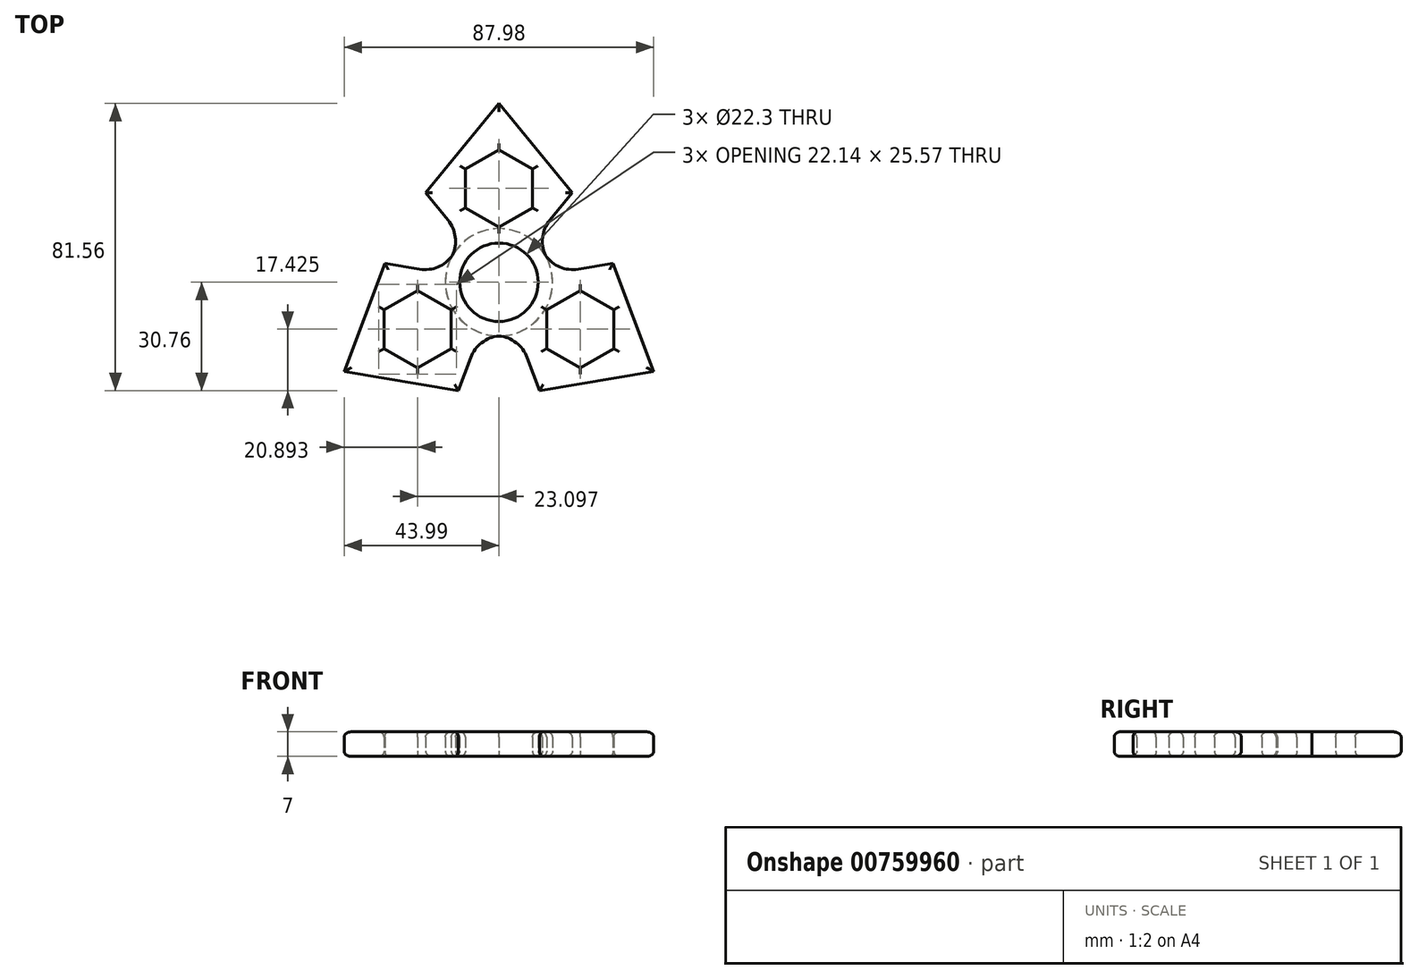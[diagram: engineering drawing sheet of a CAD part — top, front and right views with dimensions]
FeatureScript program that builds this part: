
annotation { "Feature Type Name" : "Feature", "Feature Type Description" : "" }
export const myFeature = defineFeature(function(context is Context, id is Id, definition is map)
    precondition{}
    {
        {
            var Q0;
            Q0=qCreatedBy(makeId("Top.planeOp"),FACE);
            var sketch = newSketch(context, id + "F0", { "sketchPlane" : qUnion([Q0])});
            skCircle(sketch, "E0", {"center": v(0, 0) * mm, "radius": 11.15 * mm});
            skCircle(sketch, "E1.cCircle", {"center": v(0, 26.67) * mm, "radius": 9.55 * mm, "construction": true});
            skLineSegment(sketch, "E1.0", {"start": v(9.55, 21.16) * mm, "end": v(0, 15.64) * mm});
            skLineSegment(sketch, "E1.1", {"start": v(0, 15.64) * mm, "end": v(-9.55, 21.16) * mm});
            skLineSegment(sketch, "E1.2", {"start": v(-9.55, 21.16) * mm, "end": v(-9.55, 32.18) * mm});
            skLineSegment(sketch, "E1.3", {"start": v(-9.55, 32.18) * mm, "end": v(0, 37.7) * mm});
            skLineSegment(sketch, "E1.4", {"start": v(0, 37.7) * mm, "end": v(9.55, 32.18) * mm});
            skLineSegment(sketch, "E1.5", {"start": v(9.55, 32.18) * mm, "end": v(9.55, 21.16) * mm});
            skCircle(sketch, "E2", {"center": v(0, 0) * mm, "radius": 15.24 * mm});
            skLineSegment(sketch, "E3", {"start": v(0, 50.8) * mm, "end": v(-20.85, 25.4) * mm});
            skLineSegment(sketch, "E4", {"start": v(-20.85, 25.4) * mm, "end": v(0, 0) * mm});
            skLineSegment(sketch, "E5", {"start": v(20.85, 25.4) * mm, "end": v(0, 50.8) * mm});
            skLineSegment(sketch, "E6", {"start": v(0, 0) * mm, "end": v(20.85, 25.4) * mm});
            skSolve(sketch);
        }
        {
            var Q0;
            {var subQ0=sQuery(id+"F0.wireOp",EDGE,"E1.1");Q0=makeQuery(id+"F0.imprint","IMPRINT",FACE,{"disambiguationData":[TD([[makeQuery(id+"F0.imprint","IMPRINT",EDGE,{"derivedFrom":subQ0}),1.0]])]});}
            var Q1;
            {var subQ1=sQuery(id+"F0.wireOp",EDGE,"0ElM1cGw-ABjy-hdxq-6Lkq-ngK1fqIPsj3w");var subQ3=sQuery(id+"F0.wireOp",EDGE,"E0");var subQ9=makeQuery(id+"F0.imprint","INTERSECT",VERTEX,{"disambiguationData":[OD(0.0)],"derivedFrom":[subQ3,subQ1]});Q1=makeQuery(id+"F0.imprint","IMPRINT",FACE,{"disambiguationData":[TD([[makeQuery(id+"F0.imprint","IMPRINT",EDGE,{"disambiguationData":[TD([[subQ9,1.0]])],"derivedFrom":subQ3}),-1.0]])]});}
            var Q2;
            {var subQ0=sQuery(id+"F0.wireOp",EDGE,"0ElM1cGw-ABjy-hdxq-6Lkq-ngK1fqIPsj3w");var subQ1=sQuery(id+"F0.wireOp",EDGE,"E0");var subQ2=makeQuery(id+"F0.imprint","INTERSECT",VERTEX,{"disambiguationData":[OD(0.0)],"derivedFrom":[subQ1,subQ0]});Q2=makeQuery(id+"F0.imprint","IMPRINT",FACE,{"disambiguationData":[TD([[makeQuery(id+"F0.imprint","IMPRINT",EDGE,{"disambiguationData":[TD([[subQ2,-1.0]])],"derivedFrom":subQ1}),-1.0]])]});}
            var Q3;
            {var subQ11=sQuery(id+"F0.wireOp",EDGE,"E1.2");Q3=makeQuery(id+"F0.imprint","IMPRINT",FACE,{"disambiguationData":[TD([[makeQuery(id+"F0.imprint","IMPRINT",EDGE,{"derivedFrom":subQ11}),1.0]])]});}
            extrude(context, id + "F1", {"entities" : qUnion([Q0, Q1, Q2, Q3]), "depth" : 7 * mm, "offsetDistance" : 25.4 * mm});
        }
        {
            var Q0;
            {var subQ0=sQuery(id+"F0.wireOp",EDGE,"E2");var subQ1=sQuery(id+"F0.wireOp",EDGE,"0ElM1cGw-ABjy-hdxq-6Lkq-ngK1fqIPsj3w");Q0=makeQuery(id+"F1.opExtrude","SWEPT_EDGE",EDGE,{"disambiguationData":[OSD([subQ1,subQ0]),TDD([makeQuery(id+"F0.imprint","INTERSECT",VERTEX,{"disambiguationData":[OD(0.0)],"derivedFrom":[subQ1,subQ0]})])]});}
            var Q1;
            {var subQ0=sQuery(id+"F0.wireOp",EDGE,"E2");var subQ1=sQuery(id+"F0.wireOp",EDGE,"0ElM1cGw-ABjy-hdxq-6Lkq-ngK1fqIPsj3w");Q1=makeQuery(id+"F1.opExtrude","SWEPT_EDGE",EDGE,{"disambiguationData":[OSD([subQ1,subQ0]),TDD([makeQuery(id+"F0.imprint","INTERSECT",VERTEX,{"disambiguationData":[OD(1.0)],"derivedFrom":[subQ1,subQ0]})])]});}
            fillet(context, id + "F2", {"entities" : qUnion([Q0, Q1]), "radius" : 9.52 * mm, "tangentPropagation" : true, "allowEdgeOverflow" : false});
        }
        {
            var Q0;
            Q0=makeQuery(id+"F1.opExtrude","SWEPT_BODY",BODY,{"disambiguationData":[OSD([sQuery(id+"F0.wireOp",EDGE,"E0"),sQuery(id+"F0.wireOp",EDGE,"d1f96c89-ae24-44dc-95b8-3d53eee9b90a.0"),sQuery(id+"F0.wireOp",EDGE,"E1.0"),sQuery(id+"F0.wireOp",EDGE,"E1.1"),sQuery(id+"F0.wireOp",EDGE,"E1.2"),sQuery(id+"F0.wireOp",EDGE,"E1.3"),sQuery(id+"F0.wireOp",EDGE,"E1.4"),sQuery(id+"F0.wireOp",EDGE,"E1.5"),sQuery(id+"F0.wireOp",EDGE,"6467eb64-f5fc-4fa4-b67a-5fdd80484858.0"),sQuery(id+"F0.wireOp",EDGE,"6467eb64-f5fc-4fa4-b67a-5fdd80484858.2"),sQuery(id+"F0.wireOp",EDGE,"6467eb64-f5fc-4fa4-b67a-5fdd80484858.3"),sQuery(id+"F0.wireOp",EDGE,"6467eb64-f5fc-4fa4-b67a-5fdd80484858.4"),sQuery(id+"F0.wireOp",EDGE,"6467eb64-f5fc-4fa4-b67a-5fdd80484858.5"),sQuery(id+"F0.wireOp",EDGE,"e1e534cc-2f33-4b0f-82cc-b4de4e4070e7"),sQuery(id+"F0.wireOp",EDGE,"d04765f5-1735-495e-b364-6d969f9b3d5d"),sQuery(id+"F0.wireOp",EDGE,"77a682f6-1ae9-43b9-b4da-7f019d4a444a.0"),sQuery(id+"F0.wireOp",EDGE,"27ab2300-1543-4c0a-a06e-bdf80a921956.0"),sQuery(id+"F0.wireOp",EDGE,"7b8874fc-19ec-4d05-a443-a3cdac1f19cd.filletArc"),sQuery(id+"F0.wireOp",EDGE,"lxG7lnsp-9xvN-WL6z-RJoO-r6IwSvIQtlOm"),sQuery(id+"F0.wireOp",EDGE,"8nAJOfJ4-Ij3l-DfIw-Xt9b-HZkO6DjjanfU")])]});
            var Q1;
            Q1=makeQuery(id+"F1.opExtrude","SWEPT_FACE",FACE,{"disambiguationData":[OSD([sQuery(id+"F0.wireOp",EDGE,"E0")])]});
            circularPattern(context, id + "F3", {"entities" : qUnion([Q0]), "axis" : qUnion([Q1]), "angle" : 360 * degree, "instanceCount" : 3, "equalSpace" : true});
        }
        {
            var Q0;
            Q0=makeQuery(id+"F1.opExtrude","CAP_FACE",FACE,{"disambiguationData":[OSD([sQuery(id+"F0.wireOp",EDGE,"E0"),sQuery(id+"F0.wireOp",EDGE,"E1.0"),sQuery(id+"F0.wireOp",EDGE,"E1.1"),sQuery(id+"F0.wireOp",EDGE,"E1.2"),sQuery(id+"F0.wireOp",EDGE,"E1.3"),sQuery(id+"F0.wireOp",EDGE,"E1.4"),sQuery(id+"F0.wireOp",EDGE,"E1.5"),sQuery(id+"F0.wireOp",EDGE,"E2"),sQuery(id+"F0.wireOp",EDGE,"E3"),sQuery(id+"F0.wireOp",EDGE,"E4"),sQuery(id+"F0.wireOp",EDGE,"E5"),sQuery(id+"F0.wireOp",EDGE,"E6")])],"isStart":false});
            var Q1;
            Q1=makeQuery(id+"F3.opPattern","COPY",FACE,{"derivedFrom":makeQuery(id+"F1.opExtrude","CAP_FACE",FACE,{"disambiguationData":[OSD([sQuery(id+"F0.wireOp",EDGE,"E0"),sQuery(id+"F0.wireOp",EDGE,"E1.0"),sQuery(id+"F0.wireOp",EDGE,"E1.1"),sQuery(id+"F0.wireOp",EDGE,"E1.2"),sQuery(id+"F0.wireOp",EDGE,"E1.3"),sQuery(id+"F0.wireOp",EDGE,"E1.4"),sQuery(id+"F0.wireOp",EDGE,"E1.5"),sQuery(id+"F0.wireOp",EDGE,"E2"),sQuery(id+"F0.wireOp",EDGE,"E3"),sQuery(id+"F0.wireOp",EDGE,"E4"),sQuery(id+"F0.wireOp",EDGE,"E5"),sQuery(id+"F0.wireOp",EDGE,"E6")])],"isStart":false}),"instanceName":"1"});
            var Q2;
            Q2=makeQuery(id+"F3.opPattern","COPY",FACE,{"derivedFrom":makeQuery(id+"F1.opExtrude","CAP_FACE",FACE,{"disambiguationData":[OSD([sQuery(id+"F0.wireOp",EDGE,"E0"),sQuery(id+"F0.wireOp",EDGE,"E1.0"),sQuery(id+"F0.wireOp",EDGE,"E1.1"),sQuery(id+"F0.wireOp",EDGE,"E1.2"),sQuery(id+"F0.wireOp",EDGE,"E1.3"),sQuery(id+"F0.wireOp",EDGE,"E1.4"),sQuery(id+"F0.wireOp",EDGE,"E1.5"),sQuery(id+"F0.wireOp",EDGE,"E2"),sQuery(id+"F0.wireOp",EDGE,"E3"),sQuery(id+"F0.wireOp",EDGE,"E4"),sQuery(id+"F0.wireOp",EDGE,"E5"),sQuery(id+"F0.wireOp",EDGE,"E6")])],"isStart":false}),"instanceName":"2"});
            var Q3;
            Q3=makeQuery(id+"F1.opExtrude","CAP_FACE",FACE,{"disambiguationData":[OSD([sQuery(id+"F0.wireOp",EDGE,"E0"),sQuery(id+"F0.wireOp",EDGE,"E1.0"),sQuery(id+"F0.wireOp",EDGE,"E1.1"),sQuery(id+"F0.wireOp",EDGE,"E1.2"),sQuery(id+"F0.wireOp",EDGE,"E1.3"),sQuery(id+"F0.wireOp",EDGE,"E1.4"),sQuery(id+"F0.wireOp",EDGE,"E1.5"),sQuery(id+"F0.wireOp",EDGE,"E2"),sQuery(id+"F0.wireOp",EDGE,"E3"),sQuery(id+"F0.wireOp",EDGE,"E4"),sQuery(id+"F0.wireOp",EDGE,"E5"),sQuery(id+"F0.wireOp",EDGE,"E6")])],"isStart":true});
            var Q4;
            Q4=makeQuery(id+"F3.opPattern","COPY",FACE,{"derivedFrom":makeQuery(id+"F1.opExtrude","CAP_FACE",FACE,{"disambiguationData":[OSD([sQuery(id+"F0.wireOp",EDGE,"E0"),sQuery(id+"F0.wireOp",EDGE,"E1.0"),sQuery(id+"F0.wireOp",EDGE,"E1.1"),sQuery(id+"F0.wireOp",EDGE,"E1.2"),sQuery(id+"F0.wireOp",EDGE,"E1.3"),sQuery(id+"F0.wireOp",EDGE,"E1.4"),sQuery(id+"F0.wireOp",EDGE,"E1.5"),sQuery(id+"F0.wireOp",EDGE,"E2"),sQuery(id+"F0.wireOp",EDGE,"E3"),sQuery(id+"F0.wireOp",EDGE,"E4"),sQuery(id+"F0.wireOp",EDGE,"E5"),sQuery(id+"F0.wireOp",EDGE,"E6")])],"isStart":true}),"instanceName":"2"});
            var Q5;
            Q5=makeQuery(id+"F3.opPattern","COPY",FACE,{"derivedFrom":makeQuery(id+"F1.opExtrude","CAP_FACE",FACE,{"disambiguationData":[OSD([sQuery(id+"F0.wireOp",EDGE,"E0"),sQuery(id+"F0.wireOp",EDGE,"E1.0"),sQuery(id+"F0.wireOp",EDGE,"E1.1"),sQuery(id+"F0.wireOp",EDGE,"E1.2"),sQuery(id+"F0.wireOp",EDGE,"E1.3"),sQuery(id+"F0.wireOp",EDGE,"E1.4"),sQuery(id+"F0.wireOp",EDGE,"E1.5"),sQuery(id+"F0.wireOp",EDGE,"E2"),sQuery(id+"F0.wireOp",EDGE,"E3"),sQuery(id+"F0.wireOp",EDGE,"E4"),sQuery(id+"F0.wireOp",EDGE,"E5"),sQuery(id+"F0.wireOp",EDGE,"E6")])],"isStart":true}),"instanceName":"1"});
            fillet(context, id + "F4", {"entities" : qUnion([Q0, Q1, Q2, Q3, Q4, Q5]), "radius" : 1.52 * mm, "tangentPropagation" : true, "allowEdgeOverflow" : false});
        }
    });
